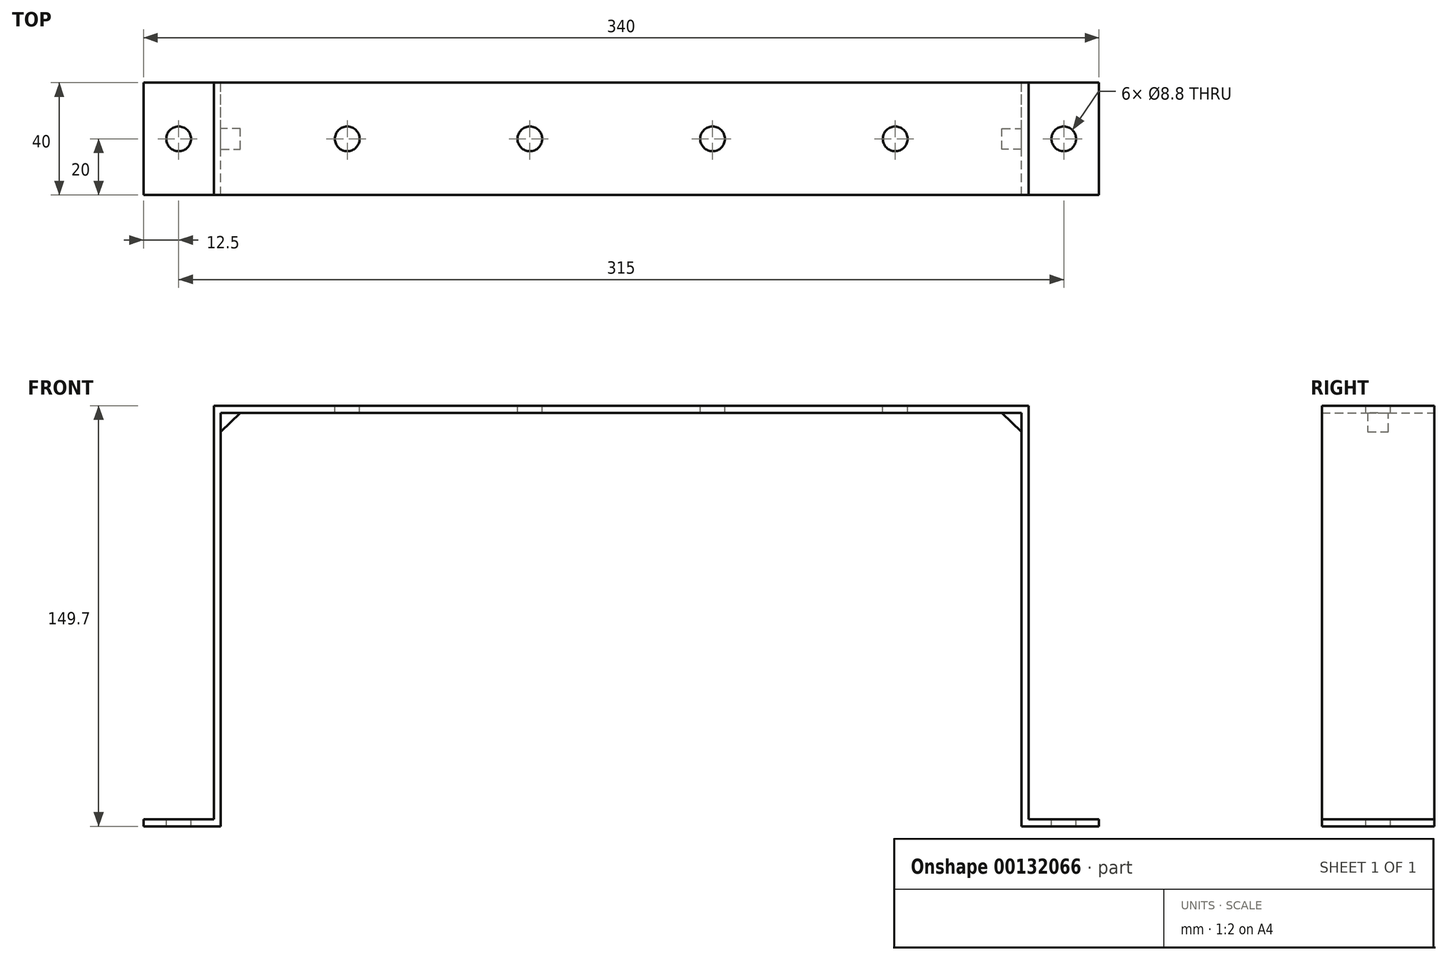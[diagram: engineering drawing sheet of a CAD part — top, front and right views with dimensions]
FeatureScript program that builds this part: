
annotation { "Feature Type Name" : "Feature", "Feature Type Description" : "" }
export const myFeature = defineFeature(function(context is Context, id is Id, definition is map)
    precondition{}
    {
        {
            var Q0;
            Q0=qCreatedBy(makeId("Front.planeOp"),FACE);
            var sketch = newSketch(context, id + "F0", { "sketchPlane" : qUnion([Q0])});
            skLineSegment(sketch, "E0.bottom", {"start": v(145, 73.6) * mm, "end": v(-145, 73.6) * mm});
            skLineSegment(sketch, "E0.left", {"start": v(145, 73.6) * mm, "end": v(145, -73.6) * mm});
            skLineSegment(sketch, "E0.right", {"start": v(-145, 73.6) * mm, "end": v(-145, -73.6) * mm});
            skPoint(sketch, "E0.middle", {"position": v(0, 0) * mm});
            skLineSegment(sketch, "E1", {"start": v(-145, -73.6) * mm, "end": v(-170, -73.6) * mm});
            skLineSegment(sketch, "E2.MirrorCS", {"start": v(145, -73.6) * mm, "end": v(170, -73.6) * mm});
            skLineSegment(sketch, "E3.0", {"start": v(-142.5, -76.1) * mm, "end": v(-170, -76.1) * mm});
            skLineSegment(sketch, "E3.1", {"start": v(142.5, -76.1) * mm, "end": v(170, -76.1) * mm});
            skLineSegment(sketch, "E3.2", {"start": v(142.5, 71.1) * mm, "end": v(142.5, -76.1) * mm});
            skLineSegment(sketch, "E3.3", {"start": v(142.5, 71.1) * mm, "end": v(-142.5, 71.1) * mm});
            skLineSegment(sketch, "E3.4", {"start": v(-142.5, 71.1) * mm, "end": v(-142.5, -76.1) * mm});
            skLineSegment(sketch, "E4", {"start": v(-170, -73.6) * mm, "end": v(-170, -76.1) * mm});
            skLineSegment(sketch, "E5", {"start": v(170, -73.6) * mm, "end": v(170, -76.1) * mm});
            skSolve(sketch);
        }
        {
            var Q0;
            Q0=makeQuery(id+"F0.imprint","IMPRINT",FACE,{"disambiguationData":[TD([[makeQuery(id+"F0.imprint","IMPRINT",EDGE,{"derivedFrom":sQuery(id+"F0.wireOp",EDGE,"E0.bottom")}),1.0]])]});
            extrude(context, id + "F1", {"entities" : qUnion([Q0]), "endBound" : BoundingType.SYMMETRIC, "depth" : 40 * mm});
        }
        {
            var Q0;
            Q0=makeQuery(id+"F1.opExtrude","SWEPT_FACE",FACE,{"disambiguationData":[OSD([sQuery(id+"F0.wireOp",EDGE,"E2.MirrorCS")])]});
            var sketch = newSketch(context, id + "F2", { "sketchPlane" : qUnion([Q0])});
            skPoint(sketch, "E6", {"position": v(157.5, 0) * mm});
            skSolve(sketch);
        }
        {
            var Q0;
            Q0=makeQuery(id+"F1.opExtrude","SWEPT_FACE",FACE,{"disambiguationData":[OSD([sQuery(id+"F0.wireOp",EDGE,"E1")])]});
            var sketch = newSketch(context, id + "F3", { "sketchPlane" : qUnion([Q0])});
            skPoint(sketch, "E7", {"position": v(-157.5, 0) * mm});
            skSolve(sketch);
        }
        {
            var Q0;
            Q0=makeQuery(id+"F1.opExtrude","SWEPT_FACE",FACE,{"disambiguationData":[OSD([sQuery(id+"F0.wireOp",EDGE,"E0.bottom")])]});
            var sketch = newSketch(context, id + "F4", { "sketchPlane" : qUnion([Q0])});
            skLineSegment(sketch, "E8", {"start": v(0, 0) * mm, "end": v(32.5, 0) * mm});
            skPoint(sketch, "E9", {"position": v(32.5, 0) * mm});
            skPoint(sketch, "E10", {"position": v(97.5, 0) * mm});
            skPoint(sketch, "E11.MirrorP", {"position": v(-32.5, 0) * mm});
            skPoint(sketch, "E12.MirrorP", {"position": v(-97.5, 0) * mm});
            skSolve(sketch);
        }
        {
            var Q0;
            Q0=sQuery(id+"F4.wireOp",VERTEX,"E12.MirrorP");
            var Q1;
            Q1=sQuery(id+"F4.wireOp",VERTEX,"E11.MirrorP");
            var Q2;
            Q2=sQuery(id+"F4.wireOp",VERTEX,"E9");
            var Q3;
            Q3=sQuery(id+"F4.wireOp",VERTEX,"E10");
            var Q4;
            Q4=sQuery(id+"F2.wireOp",VERTEX,"E6");
            var Q5;
            Q5=sQuery(id+"F3.wireOp",VERTEX,"E7");
            var Q6;
            Q6=makeQuery(id+"F1.opExtrude","SWEPT_BODY",BODY,{"disambiguationData":[OSD([sQuery(id+"F0.wireOp",EDGE,"E0.bottom"),sQuery(id+"F0.wireOp",EDGE,"E0.left"),sQuery(id+"F0.wireOp",EDGE,"E0.right"),sQuery(id+"F0.wireOp",EDGE,"E1"),sQuery(id+"F0.wireOp",EDGE,"E2.MirrorCS"),sQuery(id+"F0.wireOp",EDGE,"E3.0"),sQuery(id+"F0.wireOp",EDGE,"E3.1"),sQuery(id+"F0.wireOp",EDGE,"E3.2"),sQuery(id+"F0.wireOp",EDGE,"E3.3"),sQuery(id+"F0.wireOp",EDGE,"E3.4"),sQuery(id+"F0.wireOp",EDGE,"E4"),sQuery(id+"F0.wireOp",EDGE,"E5")])]});
            hole(context, id + "F5", {"style" : HoleStyle.SIMPLE, "endStyle" : HoleEndStyle.THROUGH, "standardTappedOrClearance" : lookupTablePath({ "standard" : "ISO", "fit" : "Normal", "size" : "M8", "type" : "Clearance" }), "standardBlindInLast" : lookupTablePath({ "fit" : "Standard", "standard" : "ISO", "size" : "M8", "type" : "Clearance" }), "holeDiameter" : 8.8 * mm, "locations" : qUnion([Q0, Q1, Q2, Q3, Q4, Q5]), "scope" : qUnion([Q6]), "isTappedThrough" : true});
        }
        {
            var Q0;
            Q0=makeQuery(id+"F1.opExtrude","SWEPT_FACE",FACE,{"disambiguationData":[OSD([sQuery(id+"F0.wireOp",EDGE,"E0.bottom")])]});
            var sketch = newSketch(context, id + "F6", { "sketchPlane" : qUnion([Q0])});
            skLineSegment(sketch, "E13.bottom", {"start": v(132.92, 3.7) * mm, "end": v(145, 3.7) * mm});
            skLineSegment(sketch, "E13.top", {"start": v(132.92, -3.7) * mm, "end": v(145, -3.7) * mm});
            skLineSegment(sketch, "E13.left", {"start": v(132.92, 3.7) * mm, "end": v(132.92, -3.7) * mm});
            skPoint(sketch, "E13.middle", {"position": v(145, 0) * mm});
            skLineSegment(sketch, "E14", {"start": v(145, -3.7) * mm, "end": v(145, 3.7) * mm});
            skSolve(sketch);
        }
        {
            var Q0;
            Q0=makeQuery(id+"F1.opExtrude","CAP_FACE",FACE,{"disambiguationData":[OSD([sQuery(id+"F0.wireOp",EDGE,"E0.bottom"),sQuery(id+"F0.wireOp",EDGE,"E0.left"),sQuery(id+"F0.wireOp",EDGE,"E0.right"),sQuery(id+"F0.wireOp",EDGE,"E1"),sQuery(id+"F0.wireOp",EDGE,"E2.MirrorCS"),sQuery(id+"F0.wireOp",EDGE,"E3.0"),sQuery(id+"F0.wireOp",EDGE,"E3.1"),sQuery(id+"F0.wireOp",EDGE,"E3.2"),sQuery(id+"F0.wireOp",EDGE,"E3.3"),sQuery(id+"F0.wireOp",EDGE,"E3.4"),sQuery(id+"F0.wireOp",EDGE,"E4"),sQuery(id+"F0.wireOp",EDGE,"E5")])],"isStart":false});
            var sketch = newSketch(context, id + "F7", { "sketchPlane" : qUnion([Q0])});
            skLineSegment(sketch, "E15", {"start": v(133.1, 73.6) * mm, "end": v(145, 62.13) * mm});
            skSolve(sketch);
        }
        {
            var Q0;
            Q0=makeQuery(id+"F6.imprint","IMPRINT",FACE,{"disambiguationData":[TD([[makeQuery(id+"F6.imprint","IMPRINT",EDGE,{"derivedFrom":sQuery(id+"F6.wireOp",EDGE,"E13.bottom")}),-1.0]])]});
            var Q1;
            Q1=sQuery(id+"F7.wireOp",EDGE,"E15");
            sweep(context, id + "F8", {"operationType" : NewBodyOperationType.ADD, "profiles" : qUnion([Q0]), "path" : qUnion([Q1])});
        }
        {
            var Q0;
            {var subQ1=sQuery(id+"F6.wireOp",EDGE,"E13.top");var subQ2=sQuery(id+"F7.wireOp",EDGE,"E15");Q0=makeQuery(id+"F8.boolean.opBoolean","SPLIT",FACE,{"disambiguationData":[TD([makeQuery(id+"F1.opExtrude","SWEPT_FACE",FACE,{"disambiguationData":[OSD([sQuery(id+"F0.wireOp",EDGE,"E0.bottom")])]})])],"derivedFrom":makeQuery(id+"F8.opSweep","SWEPT_FACE",FACE,{"disambiguationData":[OSD([subQ1,subQ2])]})});}
            extrude(context, id + "F9", {"entities" : qUnion([Q0]), "operationType" : NewBodyOperationType.REMOVE, "oppositeDirection" : true, "depth" : 25 * mm});
        }
        {
            var Q0;
            Q0=makeQuery(id+"F1.opExtrude","SWEPT_BODY",BODY,{"disambiguationData":[OSD([sQuery(id+"F0.wireOp",EDGE,"E0.bottom"),sQuery(id+"F0.wireOp",EDGE,"E0.left"),sQuery(id+"F0.wireOp",EDGE,"E0.right"),sQuery(id+"F0.wireOp",EDGE,"E1"),sQuery(id+"F0.wireOp",EDGE,"E2.MirrorCS"),sQuery(id+"F0.wireOp",EDGE,"E3.0"),sQuery(id+"F0.wireOp",EDGE,"E3.1"),sQuery(id+"F0.wireOp",EDGE,"E3.2"),sQuery(id+"F0.wireOp",EDGE,"E3.3"),sQuery(id+"F0.wireOp",EDGE,"E3.4"),sQuery(id+"F0.wireOp",EDGE,"E4"),sQuery(id+"F0.wireOp",EDGE,"E5")])]});
            var Q1;
            Q1=qCreatedBy(makeId("Right.planeOp"),FACE);
            mirror(context, id + "F10", {"operationType" : NewBodyOperationType.ADD, "entities" : qUnion([Q0]), "mirrorPlane" : qUnion([Q1])});
        }
    });
